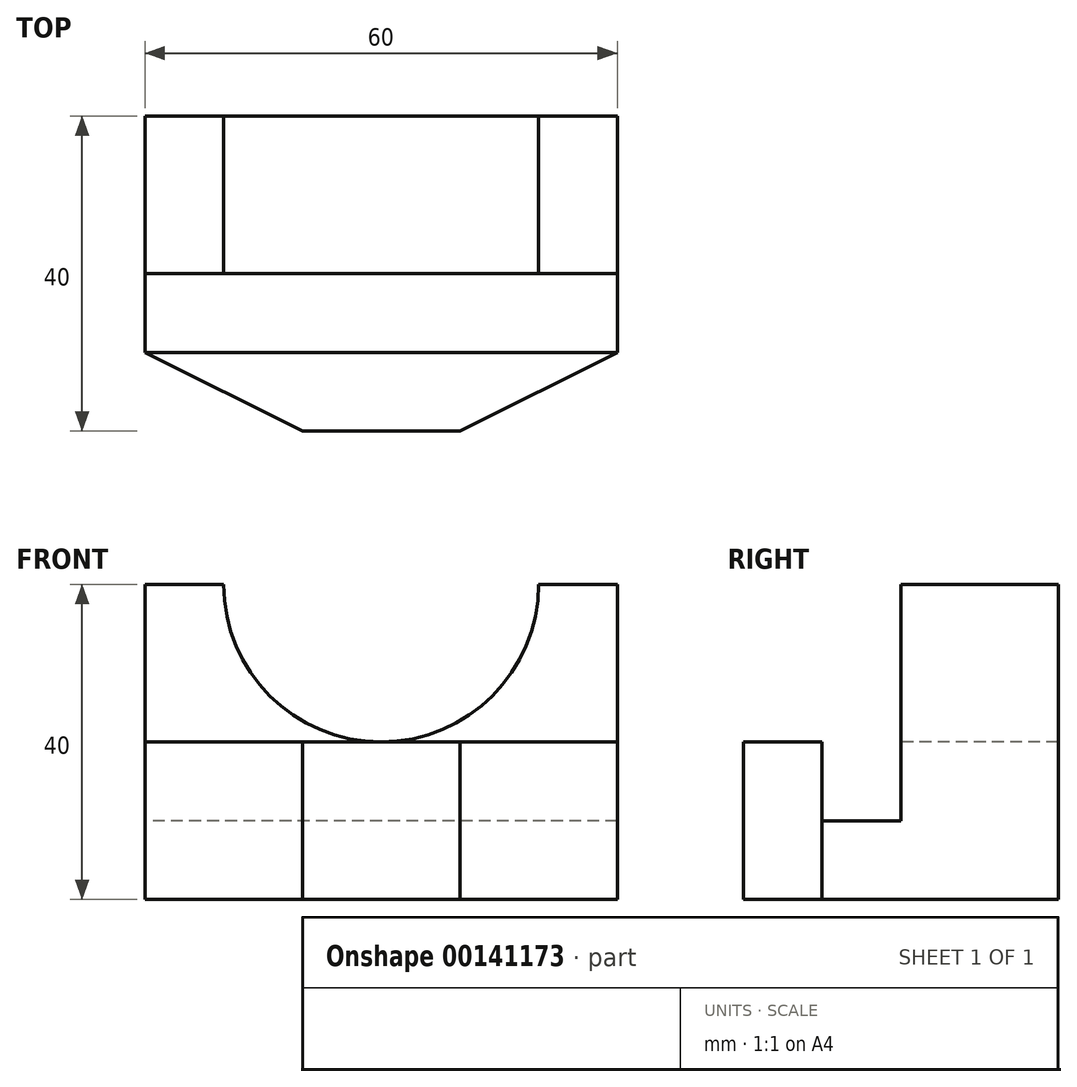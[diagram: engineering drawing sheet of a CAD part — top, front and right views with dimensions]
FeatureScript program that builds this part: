
annotation { "Feature Type Name" : "Feature", "Feature Type Description" : "" }
export const myFeature = defineFeature(function(context is Context, id is Id, definition is map)
    precondition{}
    {
        {
            var Q0;
            Q0=qCreatedBy(makeId("Top.planeOp"),FACE);
            var sketch = newSketch(context, id + "F0", { "sketchPlane" : qUnion([Q0])});
            skLineSegment(sketch, "E0", {"start": v(0, 30) * mm, "end": v(0, 0) * mm});
            skLineSegment(sketch, "E1", {"start": v(0, 0) * mm, "end": v(20, -10) * mm});
            skLineSegment(sketch, "E2", {"start": v(20, -10) * mm, "end": v(40, -10) * mm});
            skLineSegment(sketch, "E3", {"start": v(40, -10) * mm, "end": v(60, 0) * mm});
            skLineSegment(sketch, "E4", {"start": v(60, 0) * mm, "end": v(60, 30) * mm});
            skLineSegment(sketch, "E5", {"start": v(60, 30) * mm, "end": v(0, 30) * mm});
            skSolve(sketch);
        }
        {
            var Q0;
            Q0 = qSketchRegion(id + "F0", true);
            extrude(context, id + "F1", {"entities" : qUnion([Q0]), "depth" : 40 * mm});
        }
        {
            var Q0;
            Q0=makeQuery(id+"F1.opExtrude","CAP_FACE",FACE,{"disambiguationData":[OSD([sQuery(id+"F0.wireOp",EDGE,"E0"),sQuery(id+"F0.wireOp",EDGE,"E1"),sQuery(id+"F0.wireOp",EDGE,"E2"),sQuery(id+"F0.wireOp",EDGE,"E3"),sQuery(id+"F0.wireOp",EDGE,"E4"),sQuery(id+"F0.wireOp",EDGE,"E5")])],"isStart":false});
            var sketch = newSketch(context, id + "F2", { "sketchPlane" : qUnion([Q0])});
            skLineSegment(sketch, "E6", {"start": v(0, 10) * mm, "end": v(0, 0) * mm});
            skLineSegment(sketch, "E7", {"start": v(0, 0) * mm, "end": v(60, 0) * mm});
            skLineSegment(sketch, "E8", {"start": v(60, 0) * mm, "end": v(60, 10) * mm});
            skLineSegment(sketch, "E9", {"start": v(60, 10) * mm, "end": v(0, 10) * mm});
            skSolve(sketch);
        }
        {
            var Q0;
            Q0 = qSketchRegion(id + "F2", true);
            extrude(context, id + "F3", {"entities" : qUnion([Q0]), "operationType" : NewBodyOperationType.REMOVE, "oppositeDirection" : true, "depth" : 30 * mm});
        }
        {
            var Q0;
            {var subQ0=sQuery(id+"F0.wireOp",EDGE,"E1");var subQ1=sQuery(id+"F0.wireOp",EDGE,"E2");var subQ2=sQuery(id+"F0.wireOp",EDGE,"E3");Q0=makeQuery(id+"F3.boolean.opBoolean","SPLIT",FACE,{"disambiguationData":[TD([makeQuery(id+"F1.opExtrude","SWEPT_FACE",FACE,{"disambiguationData":[OSD([subQ0])]})])],"derivedFrom":makeQuery(id+"F1.opExtrude","CAP_FACE",FACE,{"disambiguationData":[OSD([sQuery(id+"F0.wireOp",EDGE,"E0"),subQ0,subQ1,subQ2,sQuery(id+"F0.wireOp",EDGE,"E4"),sQuery(id+"F0.wireOp",EDGE,"E5")])],"isStart":false})});}
            var sketch = newSketch(context, id + "F4", { "sketchPlane" : qUnion([Q0])});
            skLineSegment(sketch, "E10", {"start": v(0, 0) * mm, "end": v(60, 0) * mm});
            skLineSegment(sketch, "E11", {"start": v(60, 0) * mm, "end": v(40, -10) * mm});
            skLineSegment(sketch, "E12", {"start": v(40, -10) * mm, "end": v(20, -10) * mm});
            skLineSegment(sketch, "E13", {"start": v(20, -10) * mm, "end": v(0, 0) * mm});
            skSolve(sketch);
        }
        {
            var Q0;
            Q0 = qSketchRegion(id + "F4", true);
            extrude(context, id + "F5", {"entities" : qUnion([Q0]), "operationType" : NewBodyOperationType.REMOVE, "oppositeDirection" : true, "depth" : 20 * mm});
        }
        {
            var Q0;
            Q0=makeQuery(id+"F3.boolean.opBoolean","COPY",FACE,{"derivedFrom":makeQuery(id+"F3.opExtrude","SWEPT_FACE",FACE,{"disambiguationData":[OSD([sQuery(id+"F2.wireOp",EDGE,"E9")])]})});
            var sketch = newSketch(context, id + "F6", { "sketchPlane" : qUnion([Q0])});
            skArc(sketch, "E14", {"start": v(10, 40) * mm, "mid": v(30, 20) * mm, "end": v(50, 40) * mm});
            skLineSegment(sketch, "E15", {"start": v(50, 40) * mm, "end": v(10, 40) * mm});
            skSolve(sketch);
        }
        {
            var Q0;
            Q0 = qSketchRegion(id + "F6", true);
            extrude(context, id + "F7", {"entities" : qUnion([Q0]), "operationType" : NewBodyOperationType.REMOVE, "endBound" : BoundingType.THROUGH_ALL, "oppositeDirection" : true, "depth" : 25 * mm});
        }
    });
